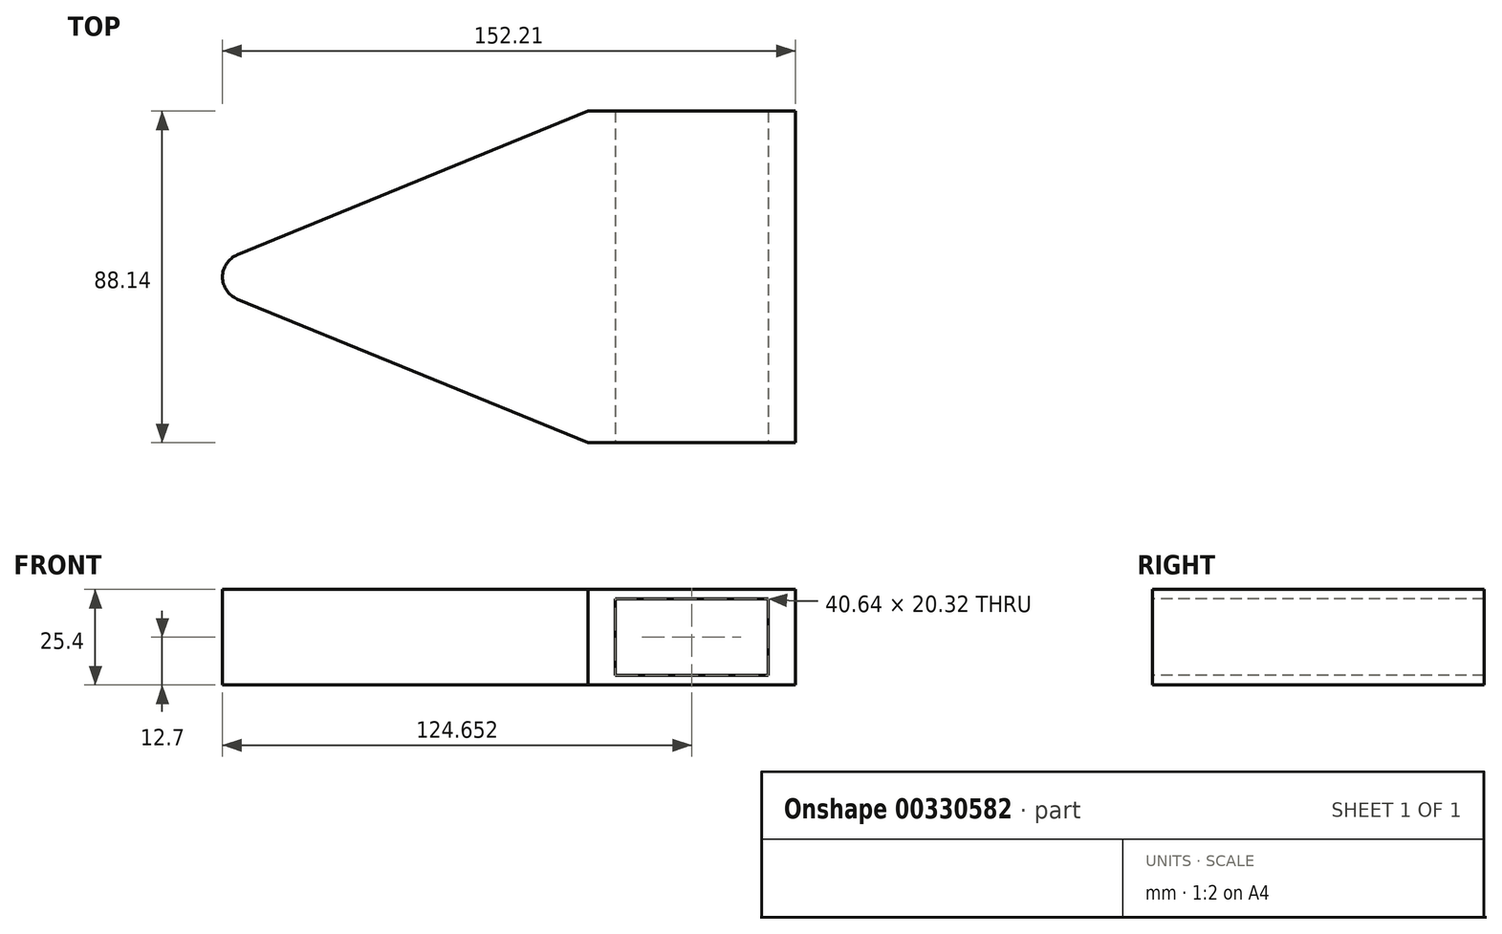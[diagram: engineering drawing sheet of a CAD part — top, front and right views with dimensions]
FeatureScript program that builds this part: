
annotation { "Feature Type Name" : "Feature", "Feature Type Description" : "" }
export const myFeature = defineFeature(function(context is Context, id is Id, definition is map)
    precondition{}
    {
        {
            var Q0;
            Q0=qCreatedBy(makeId("Top.planeOp"),FACE);
            var sketch = newSketch(context, id + "F0", { "sketchPlane" : qUnion([Q0])});
            skLineSegment(sketch, "E0", {"start": v(-114.12, 0) * mm, "end": v(123.73, 0) * mm, "construction": true});
            skLineSegment(sketch, "E1", {"start": v(0, 107.64) * mm, "end": v(0, -102.2) * mm, "construction": true});
            skLineSegment(sketch, "E2", {"start": v(-73.03, 5.88) * mm, "end": v(66.48, 63.08) * mm});
            skLineSegment(sketch, "E3", {"start": v(75.24, 57.2) * mm, "end": v(75.24, -57.2) * mm});
            skLineSegment(sketch, "E4", {"start": v(66.48, -63.08) * mm, "end": v(-73.03, -5.88) * mm});
            skPoint(sketch, "E5.visualSharp", {"position": v(75.24, 66.67) * mm});
            skArc(sketch, "E5.filletArc", {"start": v(75.24, 57.2) * mm, "mid": v(72.43, 62.48) * mm, "end": v(66.48, 63.08) * mm});
            skPoint(sketch, "E6.visualSharp", {"position": v(-87.36, 0) * mm});
            skArc(sketch, "E6.filletArc", {"start": v(-73.03, 5.88) * mm, "mid": v(-76.97, 0) * mm, "end": v(-73.03, -5.88) * mm});
            skPoint(sketch, "E7.visualSharp", {"position": v(75.24, -66.67) * mm});
            skArc(sketch, "E7.filletArc", {"start": v(66.48, -63.08) * mm, "mid": v(72.43, -62.48) * mm, "end": v(75.24, -57.2) * mm});
            skLineSegment(sketch, "E8", {"start": v(20.12, 44.07) * mm, "end": v(75.24, 44.07) * mm});
            skLineSegment(sketch, "E9.MirrorCS", {"start": v(20.12, -44.07) * mm, "end": v(75.24, -44.07) * mm});
            skSolve(sketch);
        }
        {
            var Q0;
            {var subQ0=sQuery(id+"F0.wireOp",EDGE,"E6.filletArc");Q0=makeQuery(id+"F0.imprint","IMPRINT",FACE,{"disambiguationData":[TD([[makeQuery(id+"F0.imprint","IMPRINT",EDGE,{"derivedFrom":subQ0}),1.0]])]});}
            extrude(context, id + "F1", {"entities" : qUnion([Q0]), "endBound" : BoundingType.SYMMETRIC, "depth" : 25.4 * mm});
        }
        {
            var Q0;
            Q0=makeQuery(id+"F1.opExtrude","SWEPT_FACE",FACE,{"disambiguationData":[OSD([sQuery(id+"F0.wireOp",EDGE,"E9.MirrorCS")])]});
            var sketch = newSketch(context, id + "F2", { "sketchPlane" : qUnion([Q0])});
            skLineSegment(sketch, "E10.bottom", {"start": v(68, 10.16) * mm, "end": v(27.36, 10.16) * mm});
            skLineSegment(sketch, "E10.top", {"start": v(68, -10.16) * mm, "end": v(27.36, -10.16) * mm});
            skLineSegment(sketch, "E10.left", {"start": v(68, 10.16) * mm, "end": v(68, -10.16) * mm});
            skLineSegment(sketch, "E10.right", {"start": v(27.36, 10.16) * mm, "end": v(27.36, -10.16) * mm});
            skPoint(sketch, "E10.middle", {"position": v(47.68, 0) * mm});
            skPoint(sketch, "E10.middle.positionSnap0", {"position": v(20.12, 0) * mm});
            skPoint(sketch, "E10.middle.positionSnap1", {"position": v(47.68, 12.7) * mm});
            skPoint(sketch, "E10.centerSnap0", {"position": v(20.12, 0) * mm});
            skPoint(sketch, "E10.centerSnap1", {"position": v(47.68, 12.7) * mm});
            skSolve(sketch);
        }
        {
            var Q0;
            Q0 = qSketchRegion(id + "F2", true);
            extrude(context, id + "F3", {"entities" : qUnion([Q0]), "operationType" : NewBodyOperationType.REMOVE, "endBound" : BoundingType.THROUGH_ALL, "oppositeDirection" : true, "depth" : 25.4 * mm});
        }
    });
